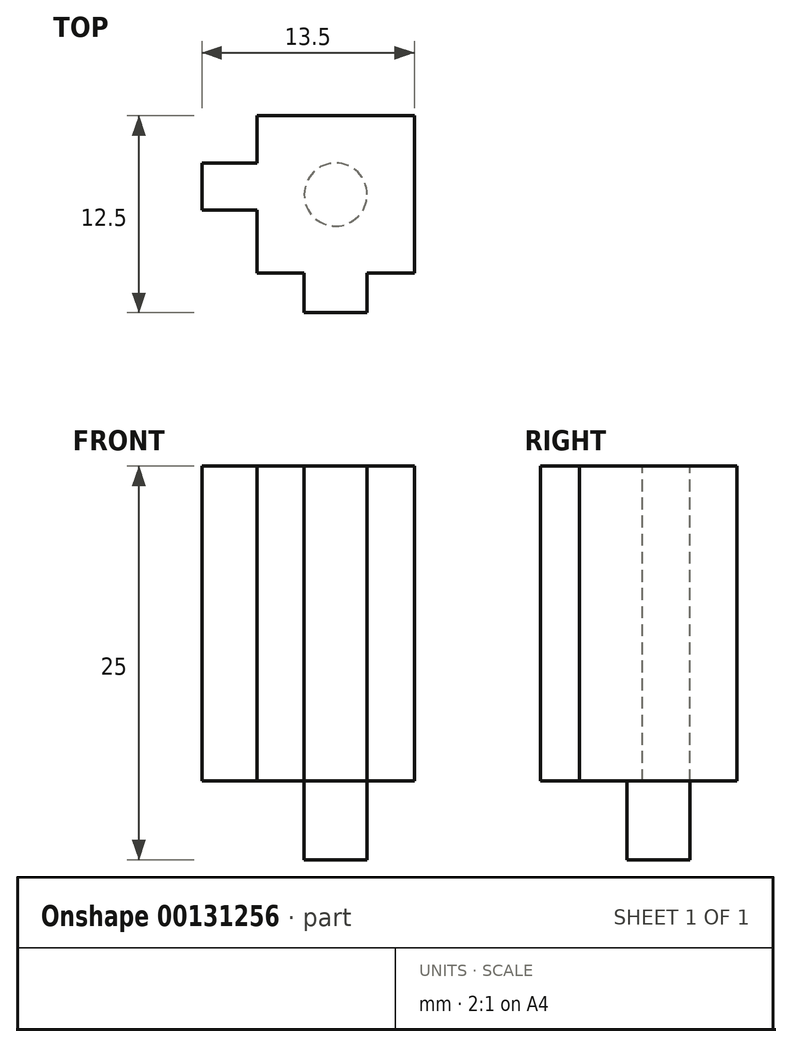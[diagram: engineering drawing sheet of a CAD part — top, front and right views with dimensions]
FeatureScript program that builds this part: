
annotation { "Feature Type Name" : "Feature", "Feature Type Description" : "" }
export const myFeature = defineFeature(function(context is Context, id is Id, definition is map)
    precondition{}
    {
        {
            var Q0;
            Q0=qCreatedBy(makeId("Top.planeOp"),FACE);
            var sketch = newSketch(context, id + "F0", { "sketchPlane" : qUnion([Q0])});
            skLineSegment(sketch, "E0", {"start": v(0, 0) * mm, "end": v(9.5, 0) * mm});
            skLineSegment(sketch, "E1", {"start": v(9.5, 0) * mm, "end": v(9.5, 10) * mm});
            skLineSegment(sketch, "E2", {"start": v(9.5, 10) * mm, "end": v(0, 10) * mm});
            skLineSegment(sketch, "E3", {"start": v(0, 10) * mm, "end": v(0, 0) * mm});
            skSolve(sketch);
        }
        {
            var Q0;
            Q0=makeQuery(id+"F0.imprint","IMPRINT",FACE,{"disambiguationData":[TD([[makeQuery(id+"F0.imprint","IMPRINT",EDGE,{"derivedFrom":sQuery(id+"F0.wireOp",EDGE,"E0")}),1.0]])]});
            extrude(context, id + "F1", {"entities" : qUnion([Q0]), "depth" : 20 * mm});
        }
        {
            var Q0;
            Q0=makeQuery(id+"F1.opExtrude","CAP_FACE",FACE,{"disambiguationData":[OSD([sQuery(id+"F0.wireOp",EDGE,"E0"),sQuery(id+"F0.wireOp",EDGE,"E1"),sQuery(id+"F0.wireOp",EDGE,"E2"),sQuery(id+"F0.wireOp",EDGE,"E3")])],"isStart":false});
            var sketch = newSketch(context, id + "F2", { "sketchPlane" : qUnion([Q0])});
            skLineSegment(sketch, "E4", {"start": v(0, 5) * mm, "end": v(9.5, 5) * mm, "construction": true});
            skLineSegment(sketch, "E5", {"start": v(0, 7) * mm, "end": v(-3.5, 7) * mm});
            skLineSegment(sketch, "E6", {"start": v(-3.5, 7) * mm, "end": v(-3.5, 4) * mm});
            skLineSegment(sketch, "E7", {"start": v(-3.5, 4) * mm, "end": v(0, 4) * mm});
            skLineSegment(sketch, "E8", {"start": v(0, 4) * mm, "end": v(0, 7) * mm});
            skLineSegment(sketch, "E9", {"start": v(5, 0) * mm, "end": v(5, 10) * mm, "construction": true});
            skCircle(sketch, "E10", {"center": v(5, 5) * mm, "radius": 2 * mm});
            skLineSegment(sketch, "E11", {"start": v(7, 0) * mm, "end": v(7, -2.5) * mm});
            skLineSegment(sketch, "E12", {"start": v(7, -2.5) * mm, "end": v(3, -2.5) * mm});
            skLineSegment(sketch, "E13", {"start": v(3, -2.5) * mm, "end": v(3, 0) * mm});
            skLineSegment(sketch, "E14", {"start": v(3, 0) * mm, "end": v(7, 0) * mm});
            skSolve(sketch);
        }
        {
            var Q0;
            Q0=makeQuery(id+"F2.imprint","IMPRINT",FACE,{"disambiguationData":[TD([[makeQuery(id+"F2.imprint","IMPRINT",EDGE,{"derivedFrom":sQuery(id+"F2.wireOp",EDGE,"5IGL5Kj7-K2Y8-aSuu-STOr-1jGKv99ohmHv")}),-1.0]])]});
            var Q1;
            Q1=makeQuery(id+"F2.imprint","IMPRINT",FACE,{"disambiguationData":[TD([[makeQuery(id+"F2.imprint","IMPRINT",EDGE,{"derivedFrom":sQuery(id+"F2.wireOp",EDGE,"E5")}),1.0]])]});
            var Q2;
            Q2=makeQuery(id+"F1.opExtrude","CAP_FACE",FACE,{"disambiguationData":[OSD([sQuery(id+"F0.wireOp",EDGE,"E0"),sQuery(id+"F0.wireOp",EDGE,"E1"),sQuery(id+"F0.wireOp",EDGE,"E2"),sQuery(id+"F0.wireOp",EDGE,"E3")])],"isStart":true});
            extrude(context, id + "F3", {"entities" : qUnion([Q0, Q1]), "operationType" : NewBodyOperationType.ADD, "endBound" : BoundingType.UP_TO_SURFACE, "oppositeDirection" : true, "endBoundEntityFace" : qUnion([Q2]), "depth" : 25 * mm});
        }
        {
            var Q0;
            {var subQ0=sQuery(id+"F0.wireOp",EDGE,"E3");var subQ1=sQuery(id+"F0.wireOp",EDGE,"E2");var subQ2=sQuery(id+"F0.wireOp",EDGE,"E1");var subQ3=sQuery(id+"F0.wireOp",EDGE,"E0");Q0=makeQuery(id+"F3.boolean.opBoolean","MERGE",FACE,{"derivedFrom":[makeQuery(id+"F1.opExtrude","CAP_FACE",FACE,{"disambiguationData":[OSD([subQ3,subQ2,subQ1,subQ0])],"isStart":true}),makeQuery(id+"F3.opExtrude","CAP_FACE",FACE,{"disambiguationData":[OSD([subQ3,subQ2,subQ1,subQ0]),ownerDisambiguation([makeQuery(id+"F3.opExtrude","SWEPT_BODY",BODY,{"disambiguationData":[OSD([sQuery(id+"F2.wireOp",EDGE,"5IGL5Kj7-K2Y8-aSuu-STOr-1jGKv99ohmHv"),sQuery(id+"F2.wireOp",EDGE,"cgtcuZT5-V6bF-xqsq-THir-DYLFeyT92R89"),sQuery(id+"F2.wireOp",EDGE,"vJMFai9f-QG5U-JeaK-5u8D-R3Ls7i3Sqg8T"),sQuery(id+"F2.wireOp",EDGE,"1Hq1ILeP-tpWc-EEZU-zeHy-o3TD9flC5vOs")])]})])],"isStart":false}),makeQuery(id+"F3.opExtrude","CAP_FACE",FACE,{"disambiguationData":[OSD([subQ3,subQ2,subQ1,subQ0]),ownerDisambiguation([makeQuery(id+"F3.opExtrude","SWEPT_BODY",BODY,{"disambiguationData":[OSD([sQuery(id+"F2.wireOp",EDGE,"E5"),sQuery(id+"F2.wireOp",EDGE,"E6"),sQuery(id+"F2.wireOp",EDGE,"E7"),sQuery(id+"F2.wireOp",EDGE,"E8")])]})])],"isStart":false})]});}
            var sketch = newSketch(context, id + "F4", { "sketchPlane" : qUnion([Q0])});
            skLineSegment(sketch, "E15", {"start": v(-3.5, -7) * mm, "end": v(-3.5, -7) * mm});
            skLineSegment(sketch, "E16", {"start": v(0, -7) * mm, "end": v(0, -4) * mm});
            skPoint(sketch, "E17", {"position": v(4.75, -10) * mm});
            skSolve(sketch);
        }
        {
            var Q0;
            Q0=makeQuery(id+"F2.imprint","IMPRINT",FACE,{"disambiguationData":[TD([[makeQuery(id+"F2.imprint","IMPRINT",EDGE,{"derivedFrom":sQuery(id+"F2.wireOp",EDGE,"E11")}),-1.0]])]});
            var Q1;
            {var subQ0=sQuery(id+"F0.wireOp",EDGE,"E3");var subQ1=sQuery(id+"F0.wireOp",EDGE,"E2");var subQ2=sQuery(id+"F0.wireOp",EDGE,"E1");var subQ3=sQuery(id+"F0.wireOp",EDGE,"E0");Q1=makeQuery(id+"F3.boolean.opBoolean","MERGE",FACE,{"derivedFrom":[makeQuery(id+"F1.opExtrude","CAP_FACE",FACE,{"disambiguationData":[OSD([subQ3,subQ2,subQ1,subQ0])],"isStart":true}),makeQuery(id+"F3.opExtrude","CAP_FACE",FACE,{"disambiguationData":[OSD([subQ3,subQ2,subQ1,subQ0])],"isStart":false})]});}
            extrude(context, id + "F5", {"entities" : qUnion([Q0]), "operationType" : NewBodyOperationType.ADD, "endBound" : BoundingType.UP_TO_SURFACE, "oppositeDirection" : true, "endBoundEntityFace" : qUnion([Q1]), "depth" : 25 * mm});
        }
        {
            var Q0;
            Q0=makeQuery(id+"F4.imprint","IMPRINT",FACE,{"disambiguationData":[TD([[makeQuery(id+"F4.imprint","IMPRINT",EDGE,{"derivedFrom":sQuery(id+"F4.wireOp",EDGE,"E16")}),-1.0]])]});
            var sketch = newSketch(context, id + "F6", { "sketchPlane" : qUnion([Q0])});
            skCircle(sketch, "E18.0", {"center": v(5, -5) * mm, "radius": 2 * mm});
            skSolve(sketch);
        }
        {
            var Q0;
            Q0 = qSketchRegion(id + "F6", true);
            extrude(context, id + "F7", {"entities" : qUnion([Q0]), "operationType" : NewBodyOperationType.ADD, "depth" : 5 * mm});
        }
        {
            var Q0;
            Q0=makeQuery(id+"F1.opExtrude","SWEPT_FACE",FACE,{"disambiguationData":[OSD([sQuery(id+"F0.wireOp",EDGE,"E1")])]});
            var sketch = newSketch(context, id + "F8", { "sketchPlane" : qUnion([Q0])});
            skSolve(sketch);
        }
        {
            var Q0;
            {var subQ0=sQuery(id+"F0.wireOp",EDGE,"E1");Q0=makeQuery(id+"F8.imprint","IMPRINT",FACE,{"disambiguationData":[TD([[makeQuery(id+"F8.imprint","IMPRINT",EDGE,{"derivedFrom":makeQuery(id+"F1.opExtrude","CAP_EDGE",EDGE,{"disambiguationData":[OSD([subQ0])],"isStart":true})}),1.0]])]});}
            extrude(context, id + "F9", {"entities" : qUnion([Q0]), "operationType" : NewBodyOperationType.ADD, "depth" : .5 * mm});
        }
    });
